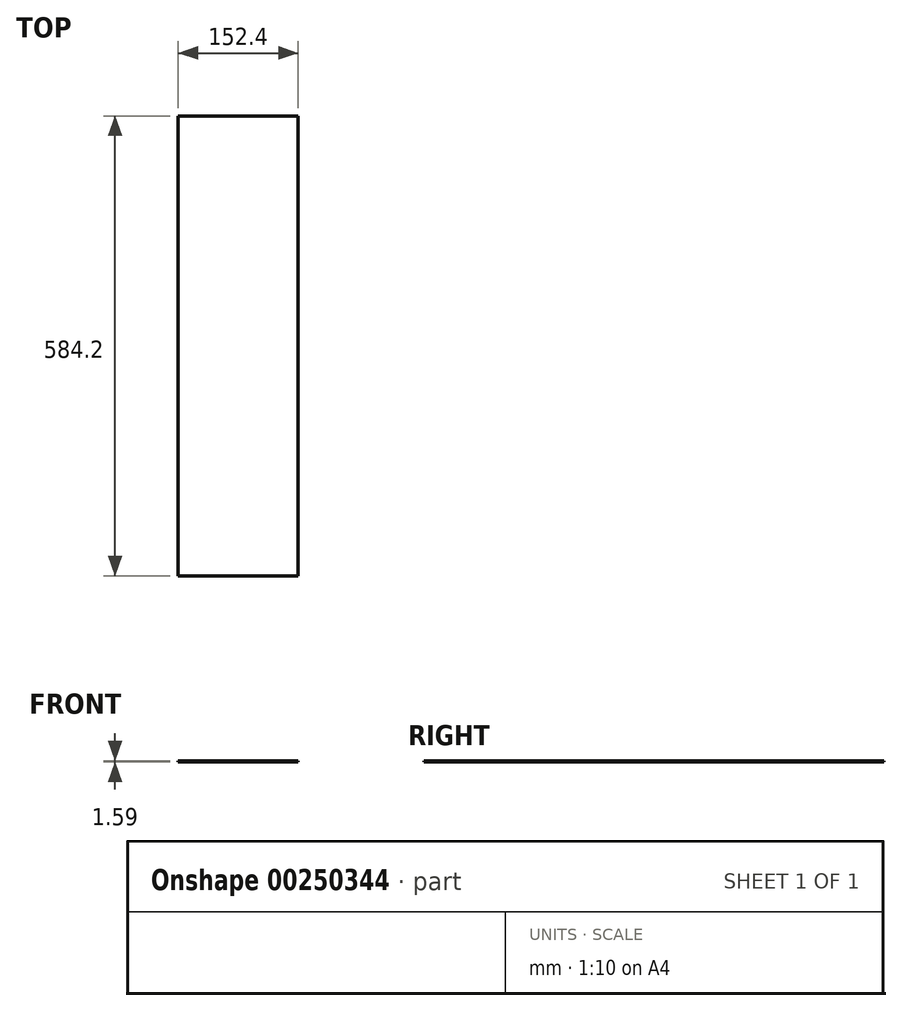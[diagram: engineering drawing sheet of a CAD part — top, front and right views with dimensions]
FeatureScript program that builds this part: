
annotation { "Feature Type Name" : "Feature", "Feature Type Description" : "" }
export const myFeature = defineFeature(function(context is Context, id is Id, definition is map)
    precondition{}
    {
        {
            var Q0;
            Q0=qCreatedBy(makeId("Top.planeOp"),FACE);
            var sketch = newSketch(context, id + "F0", { "sketchPlane" : qUnion([Q0])});
            skLineSegment(sketch, "E0.bottom", {"start": v(76.2, 292.1) * mm, "end": v(-76.2, 292.1) * mm});
            skLineSegment(sketch, "E0.top", {"start": v(76.2, -292.1) * mm, "end": v(-76.2, -292.1) * mm});
            skLineSegment(sketch, "E0.left", {"start": v(76.2, 292.1) * mm, "end": v(76.2, -292.1) * mm});
            skLineSegment(sketch, "E0.right", {"start": v(-76.2, 292.1) * mm, "end": v(-76.2, -292.1) * mm});
            skPoint(sketch, "E0.middle", {"position": v(0, 0) * mm});
            skSolve(sketch);
        }
        {
            var Q0;
            Q0 = qSketchRegion(id + "F0", true);
            extrude(context, id + "F1", {"entities" : qUnion([Q0]), "depth" : 1.59 * mm});
        }
    });
